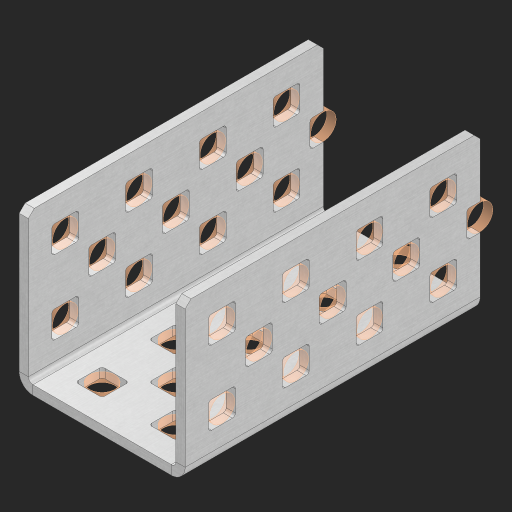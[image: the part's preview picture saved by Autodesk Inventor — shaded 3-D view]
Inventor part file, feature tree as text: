
AUTODESK INVENTOR PART (.ipt)
format: ipt  version: 2023 (Build 270158000, 158)  size: 860,160 bytes
history: native  units: in
note: dims shown in document units (in); Inventor stores cm internally (conversion verified against a paired STEP export)
features: other x54, extrude x46, sheet_metal_op x8, sketch x7, mirror x3, pattern_linear x2, chamfer x1
ambient origin geometry x8: Origin, YZ Plane, XZ Plane, XY Plane, X Axis, Y Axis, Z Axis, Center Point
bodies: Solid1 (feature_tree), Body (feature_tree)
feature tree (121):
  sheet_metal_op  "Flanges"
  sheet_metal_op  "Body Pattern"
  pattern_linear  "Center Pattern"  Spacing1=1.0in  [1 undecoded]
  other  "Arc Length"
  mirror  "Notch Mirror"
  pattern_linear  "Notch Pattern"  Spacing1=0.25in  [1 undecoded]
  other  "Diagonal Plane"
  mirror  "Flange 1"
  mirror  "Flange 2"
  chamfer  "End Chamfer"
  sketch  "Sketch1"  dims[d0=1.0in]
  other  "Plate1"
  sketch  "Sketch2"  dims[d1=2.0in]
  other  "Plate2"
  sheet_metal_op  "Bend1"
  sheet_metal_op  "Corner1"
  sketch  "Sketch8"  dims[d2=0.0625in]
  sketch  "Sketch9"  dims[d3=0.0625in]
  other  "Srf91"
  sheet_metal_op  "Body Pattern Sketch"
  other  "Srf92"
  sketch  "Sketch13"  dims[d4=0.0312in]
  sketch  "Sketch15"  dims[d5=0.125in]
  sketch  "Sketch16"  dims[d6=0.0625in d7=1.0in d8=90.0deg d9=0.0312in d10=0.25in d11=0.0625in d12=0.0625in d49=0.182in d50=0.02in d52=0.25in d53=0.0625in d54=0.0in d55=0.172in d56=1.0in d57=0.0in d60=1.5748in d62=0.5in d63=0.7874in d65=0.5in d85=0.1473in d86=0.1782in d88=0.04in d89=0.0625in d90=0.0in d91=0.04in d92=0.0491in d95=2.5in d96=0.04in d97=0.25in d98=45.0deg d99=0.25in d102=2.497in d106=0.182in d107=0.02in d108=0.5in d110=0.0625in d111=0.0in d112=0.172in d113=0.5in d114=0.0in d117=0.5in d118=0.5in d131=0.25in d132=0.25in]
  other  "Srf786"
  other  "Srf889"
  other  "Srf890"
  other  "Srf891"
  other  "Srf1315"
  other  "Srf1316"
  other  "Srf1317"
  other  "Srf1325"
  other  "Srf1326"
  other  "Srf1327"
  other  "Srf1374"
  other  "Srf1375"
  other  "Srf1376"
  other  "Srf1384"
  other  "Srf1385"
  other  "Srf1386"
  other  "Srf1433"
  other  "Srf1434"
  other  "Srf1473"
  other  "Srf1474"
  other  "Srf1475"
  other  "Srf1476"
  other  "Srf1500"
  other  "Srf1501"
  other  "Srf1502"
  other  "Srf1503"
  other  "Srf1504"
  other  "Srf1505"
  other  "Srf1538"
  other  "Srf1539"
  other  "Srf1540"
  other  "Srf1541"
  other  "Srf1542"
  other  "Srf1543"
  other  "Srf1576"
  other  "Srf1577"
  other  "Srf1578"
  other  "Srf1579"
  other  "Srf1580"
  other  "Srf1581"
  other  "Srf1614"
  other  "Srf1615"
  other  "Srf1616"
  other  "Srf1617"
  other  "Srf1618"
  other  "Srf1619"
  sheet_metal_op  "Body Stamp"
  sheet_metal_op  "Body Circle"
  other  "Center Stamp"
  other  "Center Circle"
  sheet_metal_op  "Notch"
  extrude  "ExtrusionSrf92"  Depth=0.0625in
  extrude  "ExtrusionSrf889"  Depth=0.0625in
  extrude  "ExtrusionSrf890"  Depth=0.182in
  extrude  "ExtrusionSrf891"  Depth=0.02in
  extrude  "ExtrusionSrf1315"  Depth=0.25in
  extrude  "ExtrusionSrf1316"  Depth=0.0625in
  extrude  "ExtrusionSrf1355"  TaperAngle=0.0deg  [1 undecoded]
  extrude  "ExtrusionSrf1356"  Depth=0.25in
  extrude  "ExtrusionSrf1357"  Depth=1.0in TaperAngle=0.0deg
  extrude  "ExtrusionSrf1358"  Depth=0.25in
  extrude  "ExtrusionSrf1374"  Depth=0.5in
  extrude  "ExtrusionSrf1375"  Depth=0.25in
  extrude  "ExtrusionSrf1414"  Depth=0.25in
  extrude  "ExtrusionSrf1415"  Depth=0.25in
  extrude  "ExtrusionSrf1416"  Depth=0.0625in
  extrude  "ExtrusionSrf1417"  TaperAngle=0.0deg  [1 undecoded]
  extrude  "ExtrusionSrf1433"  Depth=0.25in
  extrude  "ExtrusionSrf1434"  Depth=0.25in
  extrude  "ExtrusionSrf1473"  Depth=0.25in
  extrude  "ExtrusionSrf1474"  Depth=0.25in TaperAngle=45.0deg
  extrude  "ExtrusionSrf1475"  Depth=0.25in
  extrude  "ExtrusionSrf1476"  Depth=0.25in
  extrude  "ExtrusionSrf1500"  Depth=0.182in
  extrude  "ExtrusionSrf1501"  Depth=0.02in
  extrude  "ExtrusionSrf1502"  Depth=0.5in
  extrude  "ExtrusionSrf1503"  Depth=0.0625in
  extrude  "ExtrusionSrf1504"  TaperAngle=0.0deg  [1 undecoded]
  extrude  "ExtrusionSrf1505"  Depth=0.25in
  extrude  "ExtrusionSrf1538"  Depth=0.5in TaperAngle=0.0deg
  extrude  "ExtrusionSrf1539"  Depth=0.5in
  extrude  "ExtrusionSrf1540"  Depth=0.5in
  extrude  "ExtrusionSrf1541"  Depth=0.25in
  extrude  "ExtrusionSrf1542"  Depth=0.25in
  extrude  "ExtrusionSrf1543"  [1 undecoded]
  extrude  "ExtrusionSrf1576"  [1 undecoded]
  extrude  "ExtrusionSrf1577"  [1 undecoded]
  extrude  "ExtrusionSrf1578"  [1 undecoded]
  extrude  "ExtrusionSrf1579"  [1 undecoded]
  extrude  "ExtrusionSrf1580"  [1 undecoded]
  extrude  "ExtrusionSrf1581"  [1 undecoded]
  extrude  "ExtrusionSrf1614"  [1 undecoded]
  extrude  "ExtrusionSrf1615"  [1 undecoded]
  extrude  "ExtrusionSrf1616"  [1 undecoded]
  extrude  "ExtrusionSrf1617"  [1 undecoded]
  extrude  "ExtrusionSrf1618"  [1 undecoded]
  extrude  "ExtrusionSrf1619"  [1 undecoded]
note: 18 required parameter values undecoded (feature->parameter linkage not recoverable at this tier; creation-order binding heuristic only, values carry confidence <= 0.55)
